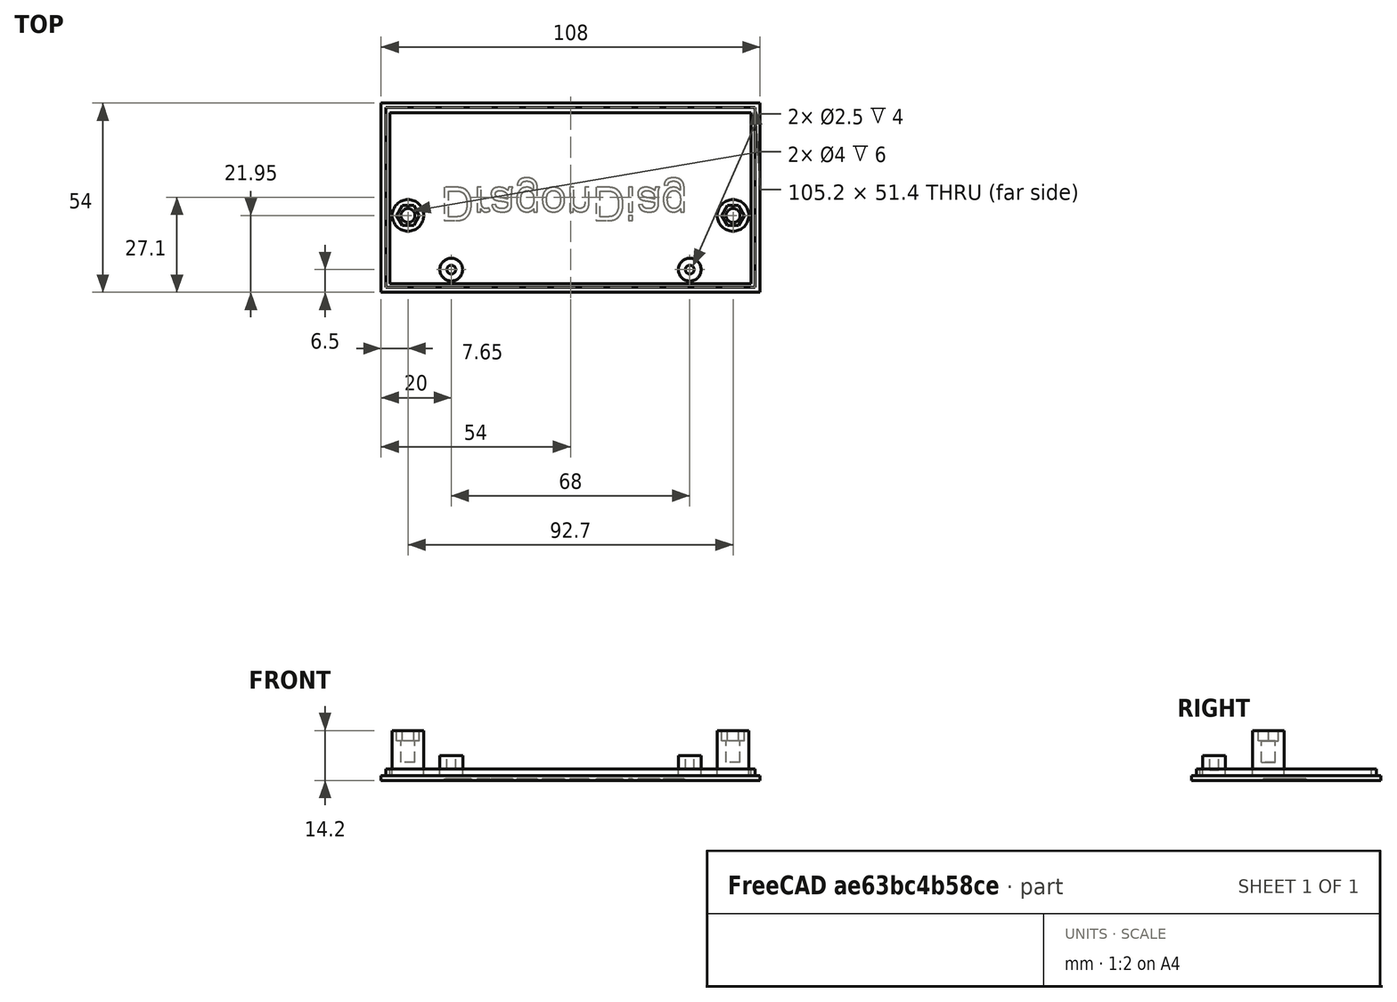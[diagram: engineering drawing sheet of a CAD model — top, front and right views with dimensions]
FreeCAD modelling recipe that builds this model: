
FCSTD DOCUMENT  (FreeCAD 0.18R4 (GitTag))
Label: DragonDiagTop-v2
License: All rights reserved
LicenseURL: http://en.wikipedia.org/wiki/All_rights_reserved
objects: Part::Cut×5, Part::Cylinder×4, Part::Box×3, Part::MultiFuse×2, Part::FeaturePython×2, Part::Extrusion×2, Part::RegularPolygon×1, Part::Part2DObjectPython×1
note: 20 computed .brp shape members not serialized (recipe doc carries the construction recipe); baked Part::Feature solids carry a one-line shape summary decoded from their .brp

FEATURE [Part::Box] Box  label="Top plate"
  AttacherType = Attacher::AttachEngine3D
  Height = 1.3
  Length = 108
  Width = 54
FEATURE [Part::Box] Box002  label="Cube002"
  AttacherType = Attacher::AttachEngine3D
  Height = 2
  Length = 103
  Placement = pos=(2.5,2.5,1.3) rot=(0,0,1;0rad)
  Width = 48.8
FEATURE [Part::Box] Box001  label="Cube001"
  AttacherType = Attacher::AttachEngine3D
  Height = 3.3
  Length = 105.2
  Placement = pos=(1.4,1.4,0) rot=(0,0,1;0rad)
  Width = 51.4
FEATURE [Part::Cut] Cut  label="Border wall"
  Base = -> Box001
  Tool = -> Box002
FEATURE [Part::MultiFuse] Fusion  label="Top plate plus wall"
  Shapes = -> [Box,Cut]
FEATURE [Part::Cylinder] Cylinder
  Angle = 360
  AttacherType = Attacher::AttachEngine3D
  Height = 7
  Placement = pos=(20,6.5,0) rot=(0,0,1;0rad)
  Radius = 3.25
FEATURE [Part::Cylinder] Cylinder001
  Angle = 360
  AttacherType = Attacher::AttachEngine3D
  Height = 4
  Placement = pos=(20,6.5,3) rot=(0,0,1;0rad)
  Radius = 1.25
FEATURE [Part::Cut] Cut002  label="Left support"
  Base = -> Cylinder
  Tool = -> Cylinder001
FEATURE [Part::FeaturePython] Clone  label="Right Support"  # Draft clone (typed FeaturePython)
  AttacherType = Attacher::AttachEngine3D
  Fuse = false
  Objects = -> [Cut002]
  Placement = pos=(68,0,0) rot=(0,0,1;0rad)
  Scale = (1,1,1)
FEATURE [Part::Cylinder] Cylinder002  label="Board Post 1"
  Angle = 360
  AttacherType = Attacher::AttachEngine3D
  Height = 14.2
  Placement = pos=(7.65,21.95,0) rot=(0,0,1;0rad)
  Radius = 4.5
FEATURE [Part::Cylinder] Cylinder003  label="Board Post 1 drill"
  Angle = 360
  AttacherType = Attacher::AttachEngine3D
  Height = 9
  Placement = pos=(7.65,21.95,5.2) rot=(0,0,1;0rad)
  Radius = 2
FEATURE [Part::Cut] Cut004  label="Board post 1 and drill"
  Base = -> Cylinder002
  Tool = -> Cylinder003
FEATURE [Part::RegularPolygon] RegularPolygon  label="Regular polygon"
  AttacherType = Attacher::AttachEngine3D
  Circumradius = 3.25
  Polygon = 6
FEATURE [Part::Extrusion] Extrude  label="M3 nut cutout"
  Base = -> RegularPolygon
  Dir = (0,0,1)
  DirMode = 0
  FaceMakerClass = Part::FaceMakerBullseye
  LengthFwd = 3
  LengthRev = 0
  Placement = pos=(7.65,21.95,11.2) rot=(0,0,1;0rad)
  Solid = true
  Symmetric = false
FEATURE [Part::Cut] Cut008  label="Board post 1 drill and nut"
  Base = -> Cut004
  Tool = -> Extrude
FEATURE [Part::FeaturePython] Clone006  label="Board post 2 drill and nut"  # Draft clone (typed FeaturePython)
  AttacherType = Attacher::AttachEngine3D
  Fuse = false
  Objects = -> [Cut008]
  Placement = pos=(92.7,0,0) rot=(0,0,1;0rad)
  Scale = (1,1,1)
FEATURE [Part::Part2DObjectPython] ShapeString  # Draft 2D object (typed FeaturePython)
  FontFile = <path>
  Size = 10
  String = DragonDiag
  Tracking = 0
FEATURE [Part::Extrusion] Extrude001  label="Name Text"
  Base = -> ShapeString
  Dir = (0,0,1)
  DirMode = 2
  FaceMakerClass = Part::FaceMakerBullseye
  LengthFwd = 0.5
  LengthRev = 0
  Placement = pos=(17,30,0.5) rot=(1,0,0;3.14159rad)
  Solid = true
  Symmetric = false
FEATURE [Part::Cut] Cut009  label="Top plate plus name"
  Base = -> Fusion
  Tool = -> Extrude001
FEATURE [Part::MultiFuse] Fusion001  label="Top plus name and posts"
  Shapes = -> [Cut002,Cut008,Cut009,Clone,Clone006]
note: 1 file-system path scrubbed to <path> (originals preserved in the JSON sidecar)
